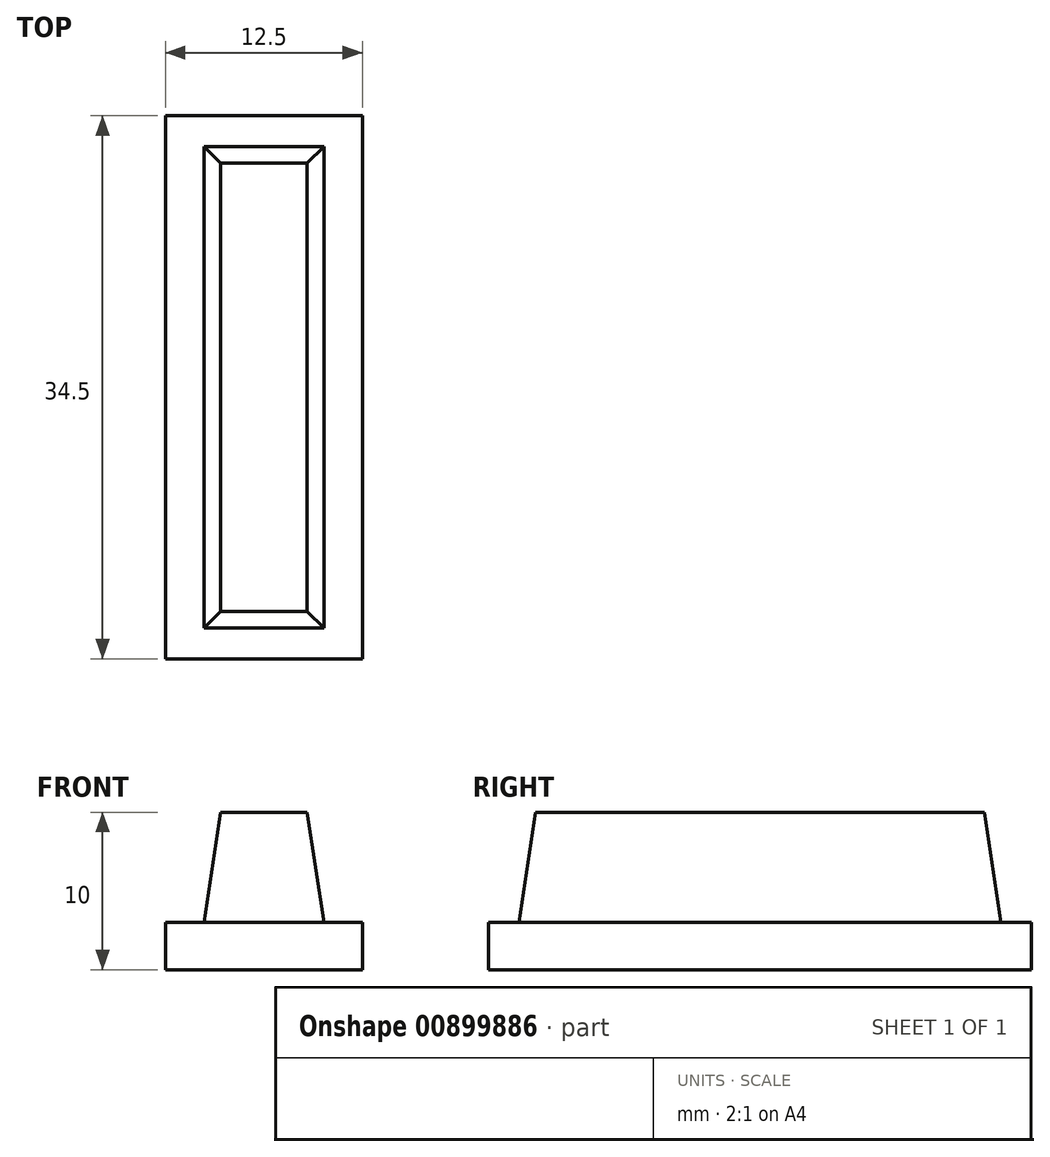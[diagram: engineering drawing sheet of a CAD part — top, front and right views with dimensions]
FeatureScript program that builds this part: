
annotation { "Feature Type Name" : "Feature", "Feature Type Description" : "" }
export const myFeature = defineFeature(function(context is Context, id is Id, definition is map)
    precondition{}
    {
        {
            var Q0;
            Q0=qCreatedBy(makeId("Top.planeOp"),FACE);
            var sketch = newSketch(context, id + "F0", { "sketchPlane" : qUnion([Q0])});
            skLineSegment(sketch, "E0.bottom", {"start": v(4.27, 15.75) * mm, "end": v(-4.26, 15.75) * mm});
            skLineSegment(sketch, "E0.top", {"start": v(4.26, -15.75) * mm, "end": v(-4.27, -15.75) * mm});
            skLineSegment(sketch, "E0.left", {"start": v(4.27, 15.75) * mm, "end": v(4.26, -15.75) * mm});
            skLineSegment(sketch, "E0.right", {"start": v(-4.26, 15.75) * mm, "end": v(-4.27, -15.75) * mm});
            skPoint(sketch, "E0.middle", {"position": v(0, 0) * mm});
            skSolve(sketch);
        }
        {
            var Q0;
            Q0=qCreatedBy(makeId("Top.planeOp"),FACE);
            cPlane(context, id + "F1", {"entities" : qUnion([Q0]), "cplaneType" : CPlaneType.OFFSET, "offset" : 10 * mm, "width" : 150 * mm, "height" : 150 * mm});
        }
        {
            var Q0;
            Q0=qCreatedBy(id+"F1.planeOp",FACE);
            var sketch = newSketch(context, id + "F2", { "sketchPlane" : qUnion([Q0])});
            skLineSegment(sketch, "E1.bottom", {"start": v(2.75, 14.25) * mm, "end": v(-2.75, 14.25) * mm});
            skLineSegment(sketch, "E1.top", {"start": v(2.75, -14.25) * mm, "end": v(-2.75, -14.25) * mm});
            skLineSegment(sketch, "E1.left", {"start": v(2.75, 14.25) * mm, "end": v(2.75, -14.25) * mm});
            skLineSegment(sketch, "E1.right", {"start": v(-2.75, 14.25) * mm, "end": v(-2.75, -14.25) * mm});
            skPoint(sketch, "E1.middle", {"position": v(0, 0) * mm});
            skSolve(sketch);
        }
        {
            var Q0;
            Q0=makeQuery(id+"F0.imprint","IMPRINT",FACE,{"disambiguationData":[TD([[makeQuery(id+"F0.imprint","IMPRINT",EDGE,{"derivedFrom":sQuery(id+"F0.wireOp",EDGE,"E0.bottom")}),1.0]])]});
            var Q1;
            Q1=makeQuery(id+"F2.imprint","IMPRINT",FACE,{"disambiguationData":[TD([[makeQuery(id+"F2.imprint","IMPRINT",EDGE,{"derivedFrom":sQuery(id+"F2.wireOp",EDGE,"E1.bottom")}),1.0]])]});
            loft(context, id + "F3", {"sheetProfilesArray" : [{ "sheetProfileEntities" : qUnion([Q0]) }, { "sheetProfileEntities" : qUnion([Q1]) }]});
        }
        {
            var Q0;
            Q0=qCreatedBy(makeId("Top.planeOp"),FACE);
            var sketch = newSketch(context, id + "F4", { "sketchPlane" : qUnion([Q0])});
            skLineSegment(sketch, "E2.bottom", {"start": v(6.25, -17.25) * mm, "end": v(-6.25, -17.25) * mm});
            skLineSegment(sketch, "E2.top", {"start": v(6.25, 17.25) * mm, "end": v(-6.25, 17.25) * mm});
            skLineSegment(sketch, "E2.left", {"start": v(6.25, -17.25) * mm, "end": v(6.25, 17.25) * mm});
            skLineSegment(sketch, "E2.right", {"start": v(-6.25, -17.25) * mm, "end": v(-6.25, 17.25) * mm});
            skPoint(sketch, "E2.middle", {"position": v(0, 0) * mm});
            skSolve(sketch);
        }
        {
            var Q0;
            Q0=makeQuery(id+"F4.imprint","IMPRINT",FACE,{"disambiguationData":[TD([[makeQuery(id+"F4.imprint","IMPRINT",EDGE,{"derivedFrom":sQuery(id+"F4.wireOp",EDGE,"E2.bottom")}),-1.0]])]});
            extrude(context, id + "F5", {"entities" : qUnion([Q0]), "operationType" : NewBodyOperationType.ADD, "depth" : 3 * mm, "offsetDistance" : 25 * mm});
        }
    });
